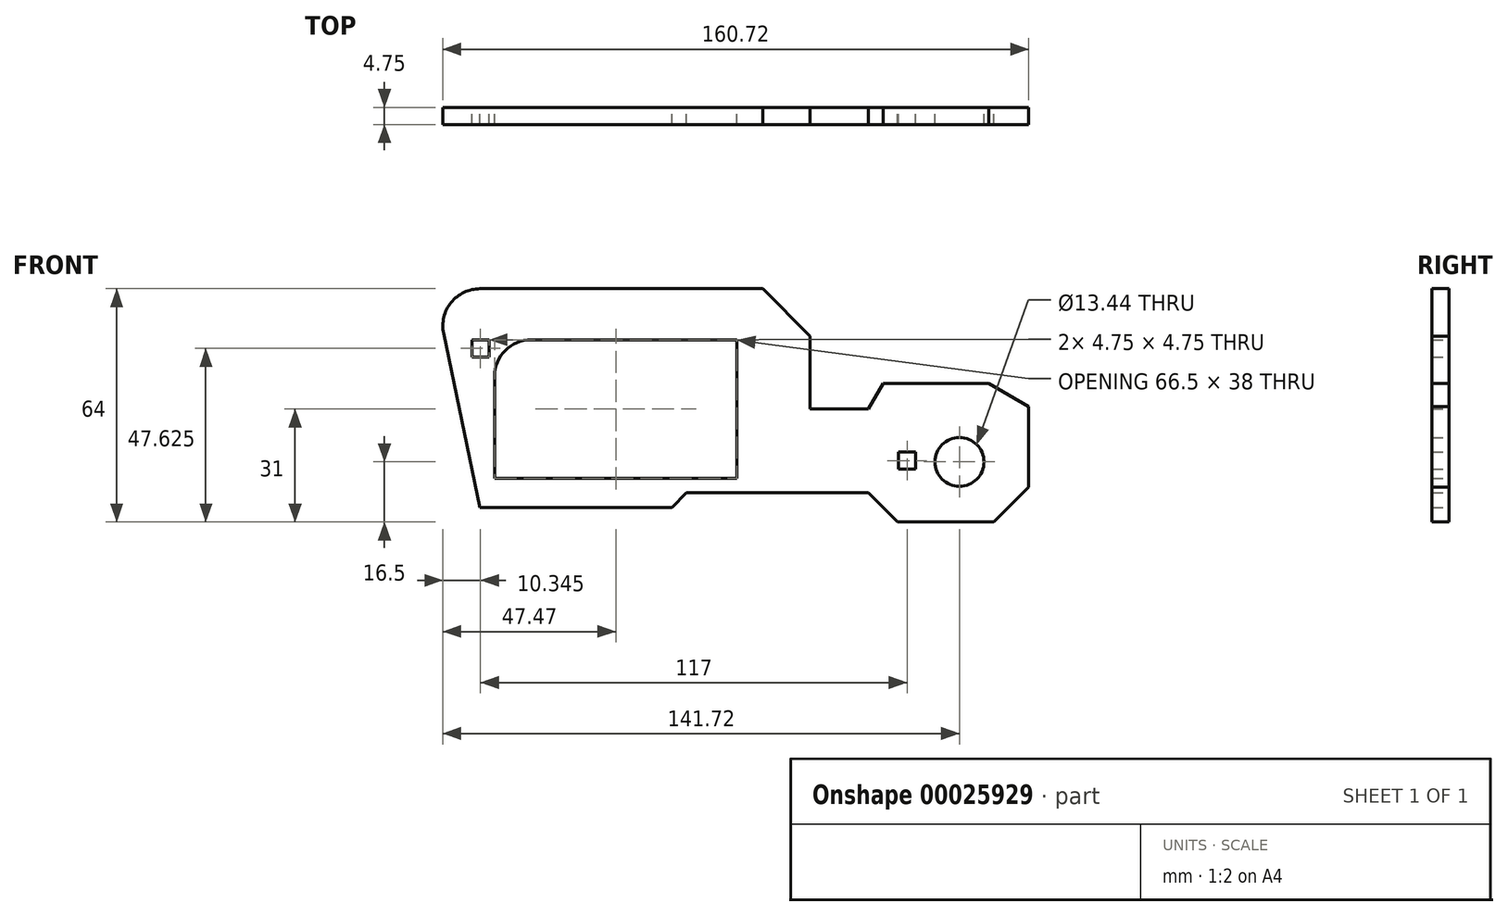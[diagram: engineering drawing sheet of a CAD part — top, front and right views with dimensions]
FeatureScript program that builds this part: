
annotation { "Feature Type Name" : "Feature", "Feature Type Description" : "" }
export const myFeature = defineFeature(function(context is Context, id is Id, definition is map)
    precondition{}
    {
        {
            var Q0;
            Q0=qCreatedBy(makeId("Front.planeOp"),FACE);
            var sketch = newSketch(context, id + "F0", { "sketchPlane" : qUnion([Q0])});
            skLineSegment(sketch, "E0.bottom", {"start": v(0, 0) * mm, "end": v(66.5, 0) * mm});
            skLineSegment(sketch, "E0.top", {"start": v(10, 38) * mm, "end": v(66.5, 38) * mm});
            skLineSegment(sketch, "E0.left", {"start": v(0, 0) * mm, "end": v(0, 28) * mm});
            skLineSegment(sketch, "E0.right", {"start": v(66.5, 0) * mm, "end": v(66.5, 38) * mm});
            skLineSegment(sketch, "E1", {"start": v(-4, -8) * mm, "end": v(48.64, -8) * mm});
            skLineSegment(sketch, "E2", {"start": v(48.64, -8) * mm, "end": v(52.64, -4) * mm});
            skLineSegment(sketch, "E3", {"start": v(52.64, -4) * mm, "end": v(102.5, -4) * mm});
            skLineSegment(sketch, "E4", {"start": v(102.5, -4) * mm, "end": v(110.5, -12) * mm});
            skLineSegment(sketch, "E5", {"start": v(110.5, -12) * mm, "end": v(136.89, -12) * mm});
            skLineSegment(sketch, "E6", {"start": v(136.89, -12) * mm, "end": v(146.5, -2.39) * mm});
            skLineSegment(sketch, "E7", {"start": v(146.5, 19.65) * mm, "end": v(135.5, 26) * mm});
            skLineSegment(sketch, "E8", {"start": v(106.54, 26) * mm, "end": v(102.5, 19) * mm});
            skLineSegment(sketch, "E9", {"start": v(102.5, 19) * mm, "end": v(86.5, 19) * mm});
            skLineSegment(sketch, "E10", {"start": v(86.5, 19) * mm, "end": v(86.5, 39) * mm});
            skLineSegment(sketch, "E11", {"start": v(86.5, 39) * mm, "end": v(83.13, 42.37) * mm});
            skLineSegment(sketch, "E12", {"start": v(73.5, 52) * mm, "end": v(-4, 52) * mm});
            skArc(sketch, "E13", {"start": v(-4, 52) * mm, "mid": v(-11.93, 48.22) * mm, "end": v(-14, 39.69) * mm});
            skLineSegment(sketch, "E14", {"start": v(-14, 39.69) * mm, "end": v(-4, -8) * mm});
            skCircle(sketch, "E15", {"center": v(127.5, 4.5) * mm, "radius": 6.72 * mm});
            skLineSegment(sketch, "E16.trimOffspring", {"start": v(77.04, 48.46) * mm, "end": v(73.5, 52) * mm});
            skLineSegment(sketch, "E17", {"start": v(77.04, 48.46) * mm, "end": v(83.13, 42.37) * mm});
            skLineSegment(sketch, "E18", {"start": v(106.54, 26) * mm, "end": v(135.5, 26) * mm});
            skLineSegment(sketch, "E19", {"start": v(146.5, 19.65) * mm, "end": v(146.5, -2.39) * mm});
            skPoint(sketch, "E20", {"position": v(127.5, 26) * mm});
            skLineSegment(sketch, "E21.bottom", {"start": v(-1.5, 38) * mm, "end": v(-6.25, 38) * mm});
            skLineSegment(sketch, "E21.top", {"start": v(-1.5, 33.25) * mm, "end": v(-6.25, 33.25) * mm});
            skLineSegment(sketch, "E21.left", {"start": v(-1.5, 38) * mm, "end": v(-1.5, 33.25) * mm});
            skLineSegment(sketch, "E21.right", {"start": v(-6.25, 38) * mm, "end": v(-6.25, 33.25) * mm});
            skLineSegment(sketch, "E22.bottom", {"start": v(110.75, 7.25) * mm, "end": v(115.5, 7.25) * mm});
            skLineSegment(sketch, "E22.top", {"start": v(110.75, 2.5) * mm, "end": v(115.5, 2.5) * mm});
            skLineSegment(sketch, "E22.left", {"start": v(110.75, 7.25) * mm, "end": v(110.75, 2.5) * mm});
            skLineSegment(sketch, "E22.right", {"start": v(115.5, 7.25) * mm, "end": v(115.5, 2.5) * mm});
            skPoint(sketch, "E23.visualSharp", {"position": v(0, 38) * mm});
            skArc(sketch, "E23.filletArc", {"start": v(10, 38) * mm, "mid": v(2.93, 35.07) * mm, "end": v(0, 28) * mm});
            skSolve(sketch);
        }
        {
            var Q0;
            Q0=qSketchRegion(id+"F0",true);
            extrude(context, id + "F1", {"entities" : qUnion([Q0]), "depth" : 4.75 * mm});
        }
    });
